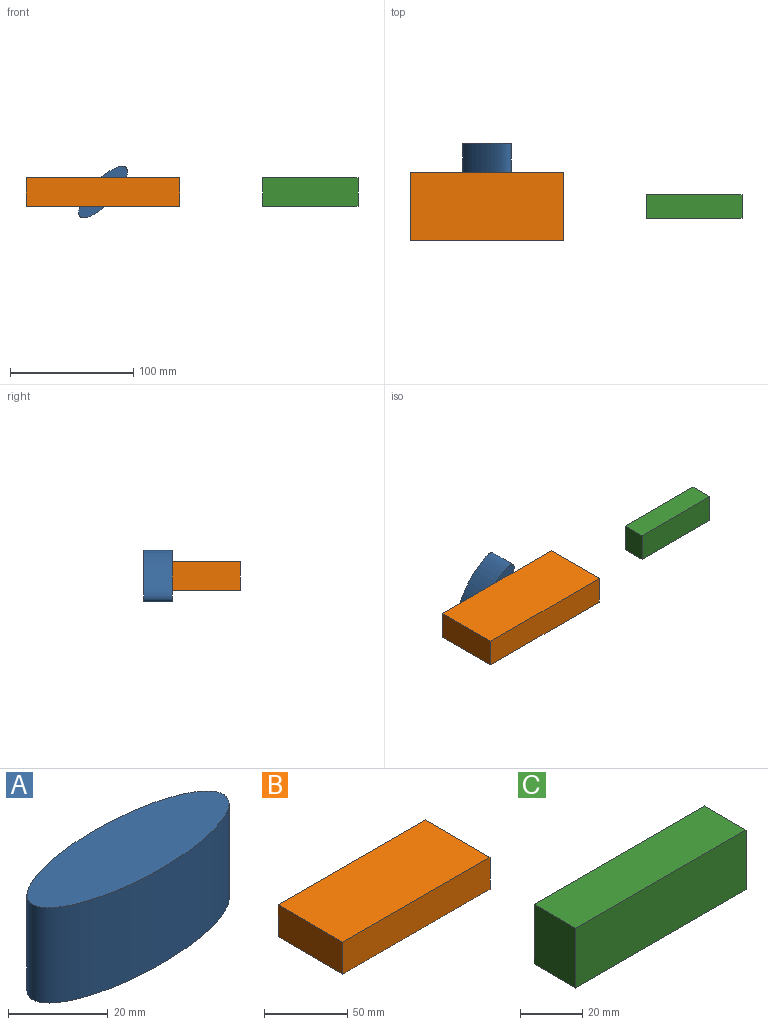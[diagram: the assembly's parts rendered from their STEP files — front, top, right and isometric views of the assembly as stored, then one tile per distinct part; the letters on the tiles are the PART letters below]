
ASSEMBLY  parts=3 mates=2
PART A: 3 faces, bbox 54.3x18.9x23.4 mm
  f0: extruded ~54.25x23.45mm, area 2855mm2, adj f1,f2
  f1: plane 54.25x18.92mm, normal (0,0,1), area 806.2mm2, adj f0
  f2: plane 54.25x18.92mm, normal (0,0,-1), area 806.2mm2, adj f0
PART B: 6 faces, bbox 124.7x55.1x23.4 mm
  f0: plane 124.7x23.45mm, normal (0,-1,0), area 2923.7mm2, adj f1,f3,f4,f5
  f1: plane 55.1x23.45mm, normal (1,0,0), area 1291.9mm2, adj f0,f2,f4,f5
  f2: plane 124.7x23.45mm, normal (0,1,0), area 2923.7mm2, adj f1,f3,f4,f5
  f3: plane 55.1x23.45mm, normal (-1,0,0), area 1291.9mm2, adj f0,f2,f4,f5
  f4: plane 124.7x55.1mm, normal (0,0,1), area 6871.2mm2, adj f0,f1,f2,f3
  f5: plane 124.7x55.1mm, normal (0,0,-1), area 6871.2mm2, adj f0,f1,f2,f3
PART C: 6 faces, bbox 77.3x19x23.4 mm
  f0: plane 77.33x23.45mm, normal (0,1,0), area 1813mm2, adj f1,f3,f4,f5
  f1: plane 23.45x18.96mm, normal (-1,0,0), area 444.5mm2, adj f0,f2,f4,f5
  f2: plane 77.33x23.45mm, normal (0,-1,0), area 1813mm2, adj f1,f3,f4,f5
  f3: plane 23.45x18.96mm, normal (1,0,0), area 444.5mm2, adj f0,f2,f4,f5
  f4: plane 77.33x18.96mm, normal (0,0,1), area 1466mm2, adj f0,f1,f2,f3
  f5: plane 77.33x18.96mm, normal (0,0,-1), area 1466mm2, adj f0,f1,f2,f3
PLACE A rot(axis=(0.29,0.68,-0.68),147.3deg) t=(-36.61,51,58.59)mm
PLACE B at identity fixed
PLACE C rot(axis=(0,1,0),180deg) t=(180.83,55.22,23.45)mm
MATE revolute B.f2 <-> A.f1  axis (0,1,0) through (0,27.55,11.72)mm
MATE slider C.f3 <-> B.f1  axis (-1,0,0) through (129.16,0,11.72)mm
